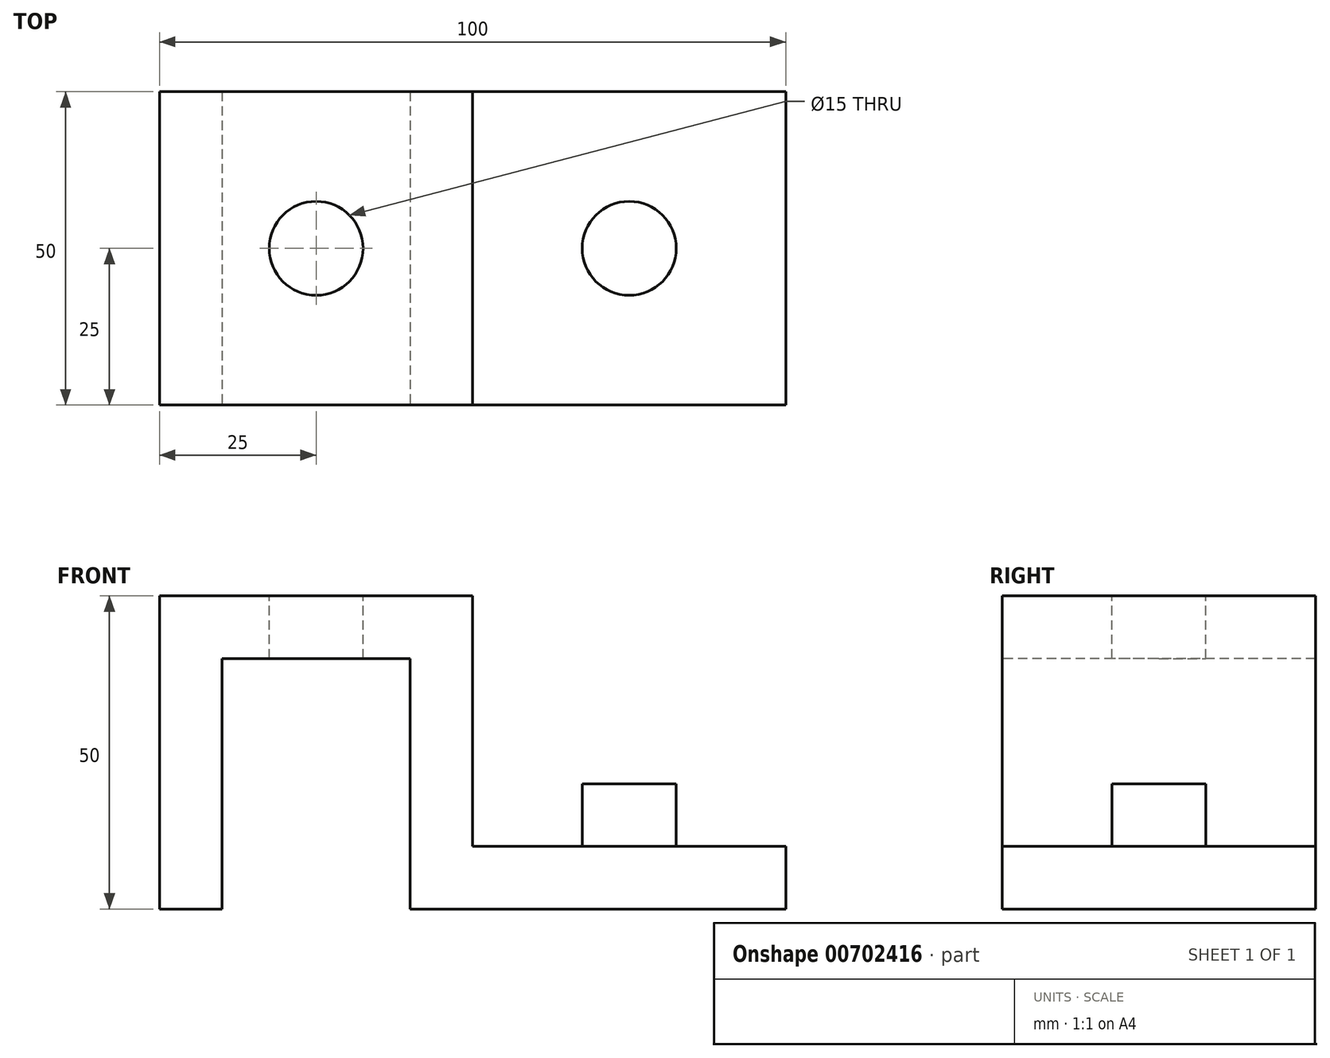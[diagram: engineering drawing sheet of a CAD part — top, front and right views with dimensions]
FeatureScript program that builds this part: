
annotation { "Feature Type Name" : "Feature", "Feature Type Description" : "" }
export const myFeature = defineFeature(function(context is Context, id is Id, definition is map)
    precondition{}
    {
        {
            var Q0;
            Q0=qCreatedBy(makeId("Front.planeOp"),FACE);
            var sketch = newSketch(context, id + "F0", { "sketchPlane" : qUnion([Q0])});
            skLineSegment(sketch, "E0.bottom", {"start": v(0, 0) * mm, "end": v(100, 0) * mm});
            skLineSegment(sketch, "E0.top", {"start": v(0, 50) * mm, "end": v(100, 50) * mm});
            skLineSegment(sketch, "E0.left", {"start": v(0, 0) * mm, "end": v(0, 50) * mm});
            skLineSegment(sketch, "E0.right", {"start": v(100, 0) * mm, "end": v(100, 50) * mm});
            skSolve(sketch);
        }
        {
            var Q0;
            Q0 = qSketchRegion(id + "F0", true);
            extrude(context, id + "F1", {"entities" : qUnion([Q0]), "oppositeDirection" : true, "depth" : 50 * mm, "offsetDistance" : 25 * mm});
        }
        {
            var Q0;
            Q0=makeQuery(id+"F1.opExtrude","CAP_FACE",FACE,{"disambiguationData":[OSD([sQuery(id+"F0.wireOp",EDGE,"E0.bottom"),sQuery(id+"F0.wireOp",EDGE,"E0.top"),sQuery(id+"F0.wireOp",EDGE,"E0.left"),sQuery(id+"F0.wireOp",EDGE,"E0.right")])],"isStart":true});
            var sketch = newSketch(context, id + "F2", { "sketchPlane" : qUnion([Q0])});
            skLineSegment(sketch, "E1.bottom", {"start": v(10, 0) * mm, "end": v(40, 0) * mm});
            skLineSegment(sketch, "E1.top", {"start": v(10, 40) * mm, "end": v(40, 40) * mm});
            skLineSegment(sketch, "E1.left", {"start": v(10, 0) * mm, "end": v(10, 40) * mm});
            skLineSegment(sketch, "E1.right", {"start": v(40, 0) * mm, "end": v(40, 40) * mm});
            skSolve(sketch);
        }
        {
            var Q0;
            Q0=makeQuery(id+"F2.imprint","IMPRINT",FACE,{"disambiguationData":[TD([[makeQuery(id+"F2.imprint","IMPRINT",EDGE,{"derivedFrom":sQuery(id+"F2.wireOp",EDGE,"E1.bottom")}),1.0]])]});
            extrude(context, id + "F3", {"entities" : qUnion([Q0]), "operationType" : NewBodyOperationType.REMOVE, "oppositeDirection" : true, "depth" : 50 * mm, "offsetDistance" : 25 * mm, "hasSecondDirection" : true, "secondDirectionOppositeDirection" : false, "secondDirectionDepth" : 25 * mm});
        }
        {
            var Q0;
            Q0=makeQuery(id+"F1.opExtrude","CAP_FACE",FACE,{"disambiguationData":[OSD([sQuery(id+"F0.wireOp",EDGE,"E0.bottom"),sQuery(id+"F0.wireOp",EDGE,"E0.top"),sQuery(id+"F0.wireOp",EDGE,"E0.left"),sQuery(id+"F0.wireOp",EDGE,"E0.right")])],"isStart":true});
            var sketch = newSketch(context, id + "F4", { "sketchPlane" : qUnion([Q0])});
            skLineSegment(sketch, "E2.bottom", {"start": v(50, 50) * mm, "end": v(100, 50) * mm});
            skLineSegment(sketch, "E2.top", {"start": v(50, 10) * mm, "end": v(100, 10) * mm});
            skLineSegment(sketch, "E2.left", {"start": v(50, 50) * mm, "end": v(50, 10) * mm});
            skLineSegment(sketch, "E2.right", {"start": v(100, 50) * mm, "end": v(100, 10) * mm});
            skSolve(sketch);
        }
        {
            var Q0;
            Q0=makeQuery(id+"F4.imprint","IMPRINT",FACE,{"disambiguationData":[TD([[makeQuery(id+"F4.imprint","IMPRINT",EDGE,{"derivedFrom":sQuery(id+"F4.wireOp",EDGE,"E2.bottom")}),-1.0]])]});
            extrude(context, id + "F5", {"entities" : qUnion([Q0]), "operationType" : NewBodyOperationType.REMOVE, "oppositeDirection" : true, "depth" : 50 * mm, "offsetDistance" : 25 * mm, "hasSecondDirection" : true, "secondDirectionOppositeDirection" : false, "secondDirectionDepth" : 25 * mm});
        }
        {
            var Q0;
            Q0=makeQuery(id+"F1.opExtrude","SWEPT_FACE",FACE,{"disambiguationData":[OSD([sQuery(id+"F0.wireOp",EDGE,"E0.top")])]});
            var sketch = newSketch(context, id + "F6", { "sketchPlane" : qUnion([Q0])});
            skCircle(sketch, "E3", {"center": v(25, 25) * mm, "radius": 7.5 * mm});
            skPoint(sketch, "E3.centerSnap0", {"position": v(25, 50) * mm});
            skSolve(sketch);
        }
        {
            var Q0;
            Q0=makeQuery(id+"F6.imprint","IMPRINT",FACE,{"disambiguationData":[TD([[makeQuery(id+"F6.imprint","IMPRINT",EDGE,{"derivedFrom":sQuery(id+"F6.wireOp",EDGE,"E3")}),1.0]])]});
            extrude(context, id + "F7", {"entities" : qUnion([Q0]), "operationType" : NewBodyOperationType.REMOVE, "endBound" : BoundingType.UP_TO_NEXT, "oppositeDirection" : true, "depth" : 25 * mm, "offsetDistance" : 25 * mm});
        }
        {
            var Q0;
            Q0=makeQuery(id+"F5.boolean.opBoolean","COPY",FACE,{"derivedFrom":makeQuery(id+"F5.opExtrude","SWEPT_FACE",FACE,{"disambiguationData":[OSD([sQuery(id+"F4.wireOp",EDGE,"E2.top")])]})});
            var sketch = newSketch(context, id + "F8", { "sketchPlane" : qUnion([Q0])});
            skLineSegment(sketch, "E4", {"start": v(50, 25) * mm, "end": v(100, 25) * mm, "construction": true});
            skCircle(sketch, "E5", {"center": v(75, 25) * mm, "radius": 7.5 * mm});
            skSolve(sketch);
        }
        {
            var Q0;
            Q0=makeQuery(id+"F8.imprint","IMPRINT",FACE,{"disambiguationData":[TD([[makeQuery(id+"F8.imprint","IMPRINT",EDGE,{"derivedFrom":sQuery(id+"F8.wireOp",EDGE,"E5")}),1.0]])]});
            extrude(context, id + "F9", {"entities" : qUnion([Q0]), "operationType" : NewBodyOperationType.ADD, "depth" : 10 * mm, "offsetDistance" : 25 * mm});
        }
    });
